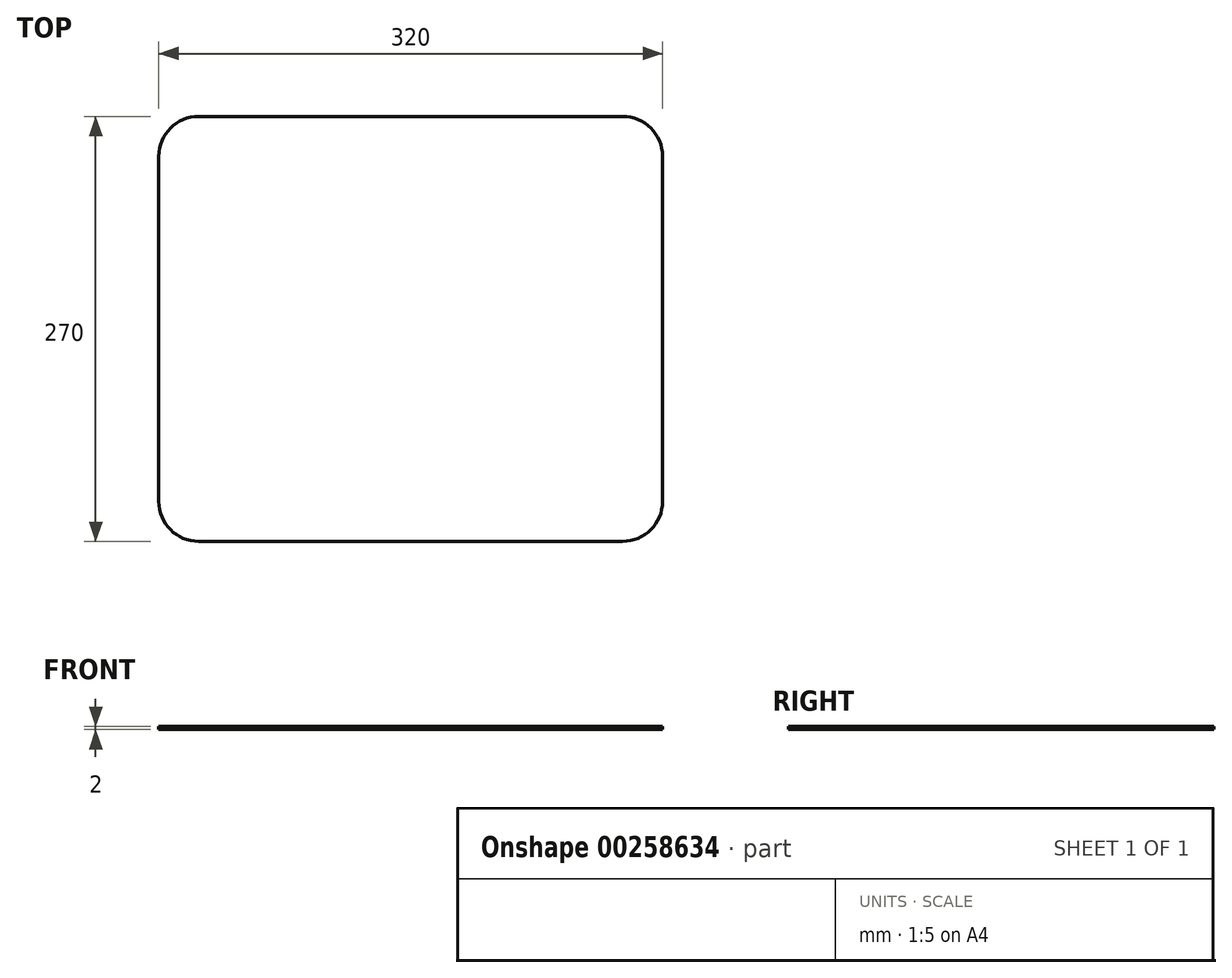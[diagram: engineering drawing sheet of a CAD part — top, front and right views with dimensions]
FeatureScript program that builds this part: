
annotation { "Feature Type Name" : "Feature", "Feature Type Description" : "" }
export const myFeature = defineFeature(function(context is Context, id is Id, definition is map)
    precondition{}
    {
        {
            var Q0;
            Q0=qCreatedBy(makeId("Top.planeOp"),FACE);
            var sketch = newSketch(context, id + "F0", { "sketchPlane" : qUnion([Q0])});
            skLineSegment(sketch, "E0.bottom", {"start": v(25.4, 0) * mm, "end": v(294.6, 0) * mm});
            skLineSegment(sketch, "E0.top", {"start": v(25.4, 270) * mm, "end": v(294.6, 270) * mm});
            skLineSegment(sketch, "E0.left", {"start": v(0, 25.4) * mm, "end": v(0, 244.6) * mm});
            skLineSegment(sketch, "E0.right", {"start": v(320, 25.4) * mm, "end": v(320, 244.6) * mm});
            skPoint(sketch, "E1.visualSharp", {"position": v(0, 270) * mm});
            skArc(sketch, "E1.filletArc", {"start": v(25.4, 270) * mm, "mid": v(7.44, 262.56) * mm, "end": v(0, 244.6) * mm});
            skPoint(sketch, "E2.visualSharp", {"position": v(0, 0) * mm});
            skArc(sketch, "E2.filletArc", {"start": v(0, 25.4) * mm, "mid": v(7.44, 7.44) * mm, "end": v(25.4, 0) * mm});
            skPoint(sketch, "E3.visualSharp", {"position": v(320, 0) * mm});
            skArc(sketch, "E3.filletArc", {"start": v(294.6, 0) * mm, "mid": v(312.56, 7.44) * mm, "end": v(320, 25.4) * mm});
            skPoint(sketch, "E4.visualSharp", {"position": v(320, 270) * mm});
            skArc(sketch, "E4.filletArc", {"start": v(320, 244.6) * mm, "mid": v(312.56, 262.56) * mm, "end": v(294.6, 270) * mm});
            skSolve(sketch);
        }
        {
            var Q0;
            Q0 = qSketchRegion(id + "F0", true);
            extrude(context, id + "F1", {"entities" : qUnion([Q0]), "depth" : 2 * mm});
        }
    });
